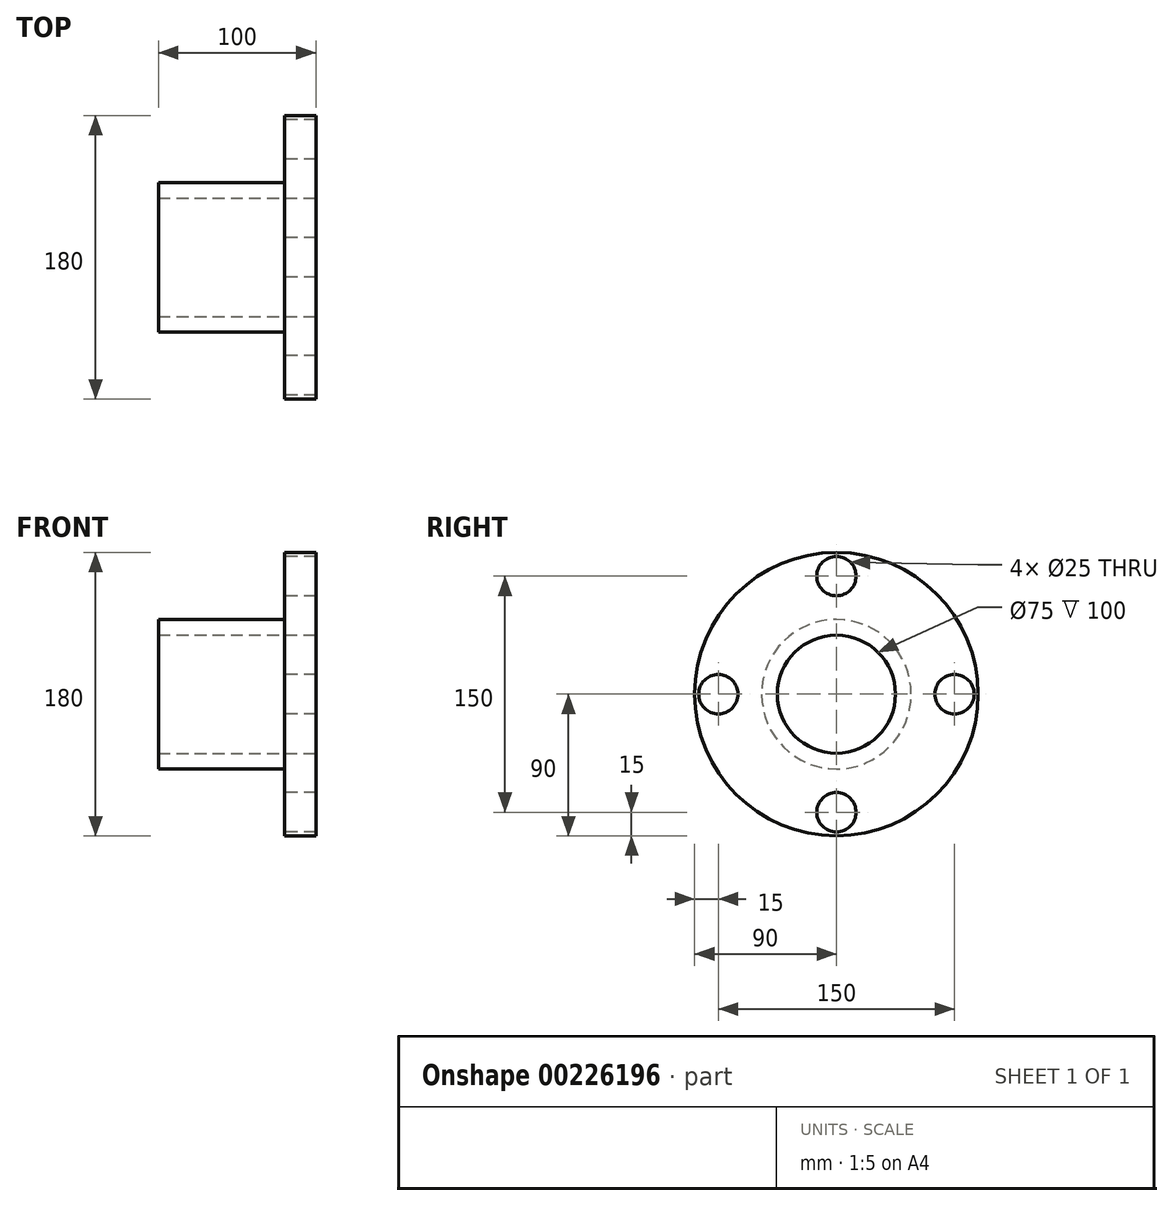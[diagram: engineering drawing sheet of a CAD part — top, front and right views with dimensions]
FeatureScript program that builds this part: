
annotation { "Feature Type Name" : "Feature", "Feature Type Description" : "" }
export const myFeature = defineFeature(function(context is Context, id is Id, definition is map)
    precondition{}
    {
        {
            var Q0;
            Q0=qCreatedBy(makeId("Front.planeOp"),FACE);
            var sketch = newSketch(context, id + "F0", { "sketchPlane" : qUnion([Q0])});
            skLineSegment(sketch, "E0", {"start": v(0, 0) * mm, "end": v(-175.37, 0) * mm, "construction": true});
            skLineSegment(sketch, "E1", {"start": v(0, 37.5) * mm, "end": v(0, 90) * mm});
            skLineSegment(sketch, "E2", {"start": v(0, 90) * mm, "end": v(-20, 90) * mm});
            skLineSegment(sketch, "E3", {"start": v(-20, 90) * mm, "end": v(-20, 47.5) * mm});
            skLineSegment(sketch, "E4", {"start": v(-20, 47.5) * mm, "end": v(-100, 47.5) * mm});
            skLineSegment(sketch, "E5", {"start": v(-100, 47.5) * mm, "end": v(-100, 37.5) * mm});
            skLineSegment(sketch, "E6", {"start": v(-100, 37.5) * mm, "end": v(0, 37.5) * mm});
            skSolve(sketch);
        }
        {
            var Q0;
            Q0=makeQuery(id+"F0.imprint","IMPRINT",FACE,{"disambiguationData":[TD([[makeQuery(id+"F0.imprint","IMPRINT",EDGE,{"derivedFrom":sQuery(id+"F0.wireOp",EDGE,"E1")}),1.0]])]});
            var Q1;
            Q1=sQuery(id+"F0.wireOp",EDGE,"E0");
            revolve(context, id + "F1", {"entities" : qUnion([Q0]), "axis" : qUnion([Q1]), "revolveType" : RevolveType.FULL});
        }
        {
            var Q0;
            Q0=makeQuery(id+"F1.opRevolve","SWEPT_FACE",FACE,{"disambiguationData":[OSD([sQuery(id+"F0.wireOp",EDGE,"E3")])]});
            var sketch = newSketch(context, id + "F2", { "sketchPlane" : qUnion([Q0])});
            skLineSegment(sketch, "E7", {"start": v(0, 90) * mm, "end": v(0, -90) * mm, "construction": true});
            skCircle(sketch, "E8", {"center": v(0, 75) * mm, "radius": 12.5 * mm});
            skCircle(sketch, "E9", {"center": v(0, 0) * mm, "radius": 75 * mm, "construction": true});
            skCircle(sketch, "E10.1.0", {"center": v(-75, 0) * mm, "radius": 12.5 * mm});
            skCircle(sketch, "E10.2.0", {"center": v(0, -75) * mm, "radius": 12.5 * mm});
            skCircle(sketch, "E10.3.0", {"center": v(75, 0) * mm, "radius": 12.5 * mm});
            skSolve(sketch);
        }
        {
            var Q0;
            Q0 = qSketchRegion(id + "F2", true);
            extrude(context, id + "F3", {"entities" : qUnion([Q0]), "operationType" : NewBodyOperationType.REMOVE, "oppositeDirection" : true, "depth" : 25 * mm});
        }
    });
